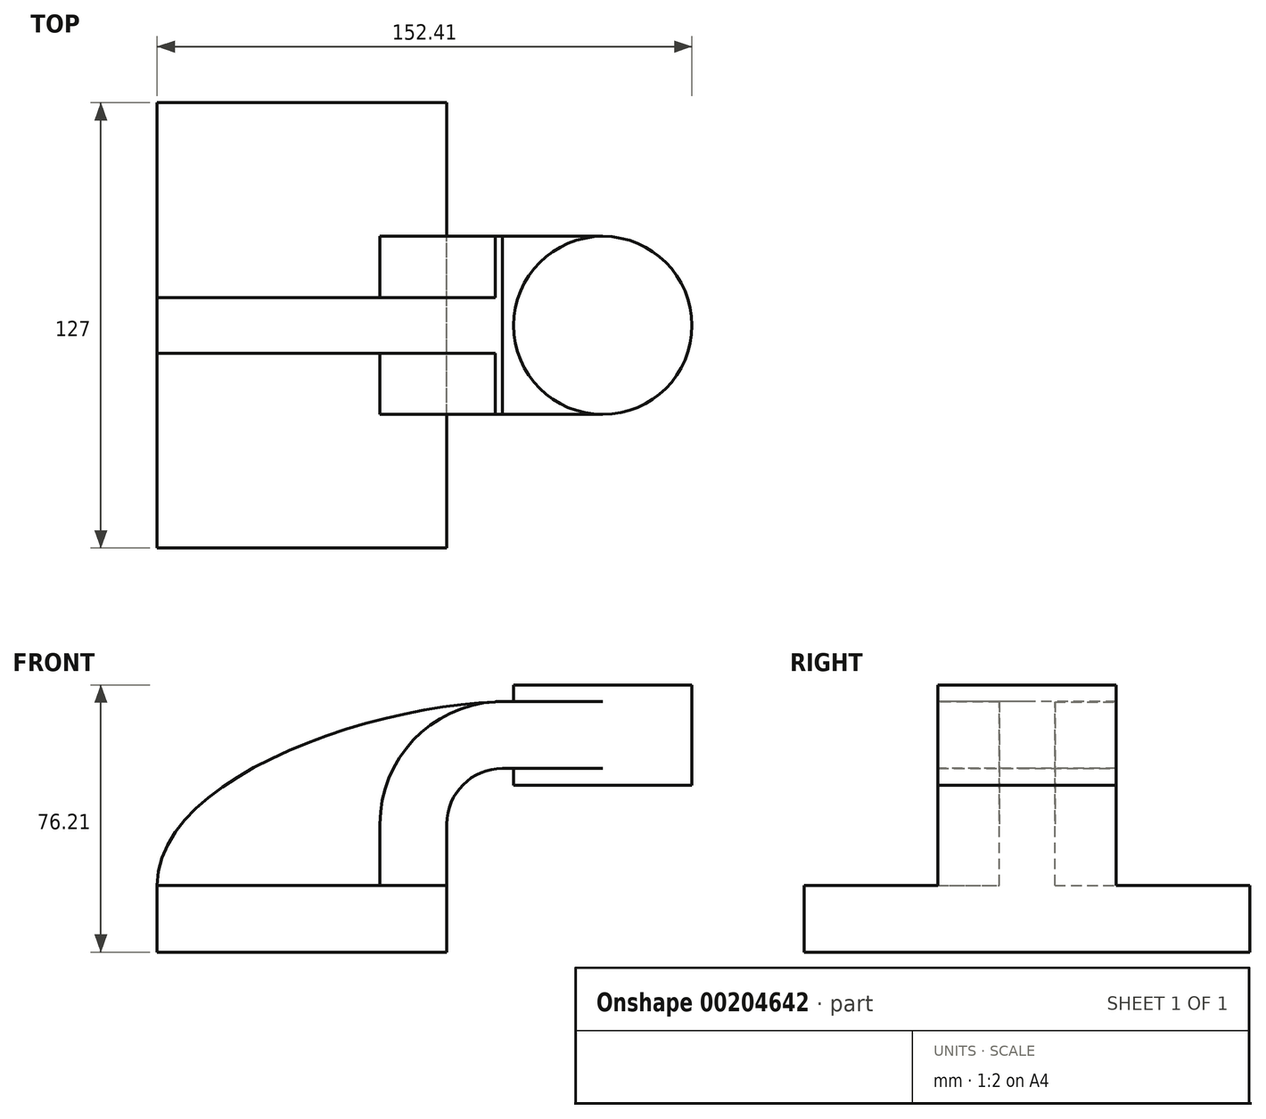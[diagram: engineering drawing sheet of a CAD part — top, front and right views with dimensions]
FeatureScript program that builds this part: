
annotation { "Feature Type Name" : "Feature", "Feature Type Description" : "" }
export const myFeature = defineFeature(function(context is Context, id is Id, definition is map)
    precondition{}
    {
        {
            var Q0;
            Q0=qCreatedBy(makeId("Front.planeOp"),FACE);
            var sketch = newSketch(context, id + "F0", { "sketchPlane" : qUnion([Q0])});
            skLineSegment(sketch, "E0.bottom", {"start": v(41.28, -9.52) * mm, "end": v(-41.28, -9.53) * mm});
            skLineSegment(sketch, "E0.top", {"start": v(41.27, 9.53) * mm, "end": v(-41.28, 9.53) * mm});
            skLineSegment(sketch, "E0.left", {"start": v(41.28, -9.52) * mm, "end": v(41.28, 9.53) * mm});
            skLineSegment(sketch, "E0.right", {"start": v(-41.28, -9.53) * mm, "end": v(-41.28, 9.53) * mm});
            skPoint(sketch, "E0.middle", {"position": v(0, 0) * mm});
            skLineSegment(sketch, "E1.bottom", {"start": v(60.33, 38.1) * mm, "end": v(111.12, 38.1) * mm});
            skLineSegment(sketch, "E1.top", {"start": v(60.32, 66.68) * mm, "end": v(111.12, 66.68) * mm});
            skLineSegment(sketch, "E1.left", {"start": v(60.33, 38.1) * mm, "end": v(60.32, 66.68) * mm});
            skLineSegment(sketch, "E1.right", {"start": v(111.12, 38.1) * mm, "end": v(111.12, 66.68) * mm});
            skPoint(sketch, "E1.middle", {"position": v(85.72, 52.39) * mm});
            skLineSegment(sketch, "E2", {"start": v(41.27, 9.53) * mm, "end": v(41.27, 26.99) * mm});
            skArc(sketch, "E3", {"start": v(41.27, 26.99) * mm, "mid": v(45.92, 38.21) * mm, "end": v(57.15, 42.86) * mm});
            skLineSegment(sketch, "E4", {"start": v(57.15, 42.86) * mm, "end": v(85.72, 42.86) * mm});
            skLineSegment(sketch, "E5.0", {"start": v(57.15, 61.91) * mm, "end": v(85.72, 61.91) * mm});
            skArc(sketch, "E5.1", {"start": v(22.23, 26.99) * mm, "mid": v(32.45, 51.68) * mm, "end": v(57.15, 61.91) * mm});
            skLineSegment(sketch, "E5.2", {"start": v(22.23, 9.53) * mm, "end": v(22.23, 26.99) * mm});
            skPoint(sketch, "E6.orphan", {"position": v(85.72, 38.1) * mm});
            skFitSpline(sketch, "E7", {"points": [v(-41.28, 9.53) * mm, v(57.15, 61.91) * mm], "startDerivative": vector(0.74, 94.84) * mm, "endDerivative": vector(105.52, 2.03) * mm});
            skLineSegment(sketch, "E8", {"start": v(85.72, 38.1) * mm, "end": v(85.72, 66.68) * mm});
            skSolve(sketch);
        }
        {
            var Q0;
            Q0=makeQuery(id+"F0.imprint","IMPRINT",FACE,{"disambiguationData":[TD([[makeQuery(id+"F0.imprint","IMPRINT",EDGE,{"derivedFrom":sQuery(id+"F0.wireOp",EDGE,"E0.bottom")}),-1.0]])]});
            extrude(context, id + "F1", {"entities" : qUnion([Q0]), "endBound" : BoundingType.SYMMETRIC, "depth" : 127 * mm});
        }
        {
            var Q0;
            {var subQ1=sQuery(id+"F0.wireOp",EDGE,"E2");Q0=makeQuery(id+"F0.imprint","IMPRINT",FACE,{"disambiguationData":[TD([[makeQuery(id+"F0.imprint","IMPRINT",EDGE,{"derivedFrom":subQ1}),1.0]])]});}
            var Q1;
            {var subQ0=sQuery(id+"F0.wireOp",EDGE,"E4");var subQ1=sQuery(id+"F0.wireOp",EDGE,"E1.left");var subQ2=makeQuery(id+"F0.imprint","INTERSECT",VERTEX,{"derivedFrom":[subQ1,subQ0]});Q1=makeQuery(id+"F0.imprint","IMPRINT",FACE,{"disambiguationData":[TD([[makeQuery(id+"F0.imprint","IMPRINT",EDGE,{"disambiguationData":[TD([[subQ2,-1.0]])],"derivedFrom":subQ1}),-1.0]])]});}
            extrude(context, id + "F2", {"entities" : qUnion([Q0, Q1]), "operationType" : NewBodyOperationType.ADD, "endBound" : BoundingType.SYMMETRIC, "depth" : 50.8 * mm});
        }
        {
            var Q0;
            {var subQ3=sQuery(id+"F0.wireOp",EDGE,"E5.2");Q0=makeQuery(id+"F0.imprint","IMPRINT",FACE,{"disambiguationData":[TD([[makeQuery(id+"F0.imprint","IMPRINT",EDGE,{"derivedFrom":subQ3}),1.0]])]});}
            extrude(context, id + "F3", {"entities" : qUnion([Q0]), "operationType" : NewBodyOperationType.ADD, "endBound" : BoundingType.SYMMETRIC, "depth" : 15.88 * mm});
        }
        {
            var Q0;
            {var subQ0=sQuery(id+"F0.wireOp",EDGE,"E1.right");Q0=makeQuery(id+"F0.imprint","IMPRINT",FACE,{"disambiguationData":[TD([[makeQuery(id+"F0.imprint","IMPRINT",EDGE,{"derivedFrom":subQ0}),1.0]])]});}
            var Q1;
            Q1=sQuery(id+"F0.wireOp",EDGE,"E8");
            revolve(context, id + "F4", {"operationType" : NewBodyOperationType.ADD, "entities" : qUnion([Q0]), "axis" : qUnion([Q1]), "revolveType" : RevolveType.FULL});
        }
    });
